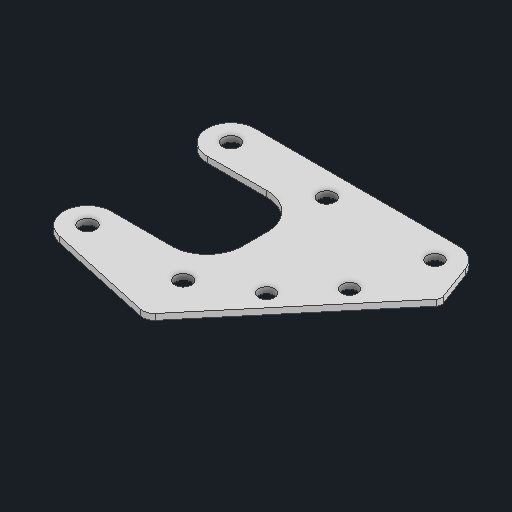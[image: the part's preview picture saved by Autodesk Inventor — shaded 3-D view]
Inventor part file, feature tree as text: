
AUTODESK INVENTOR PART (.ipt)
format: ipt  version: 2025 (Build 290162000, 162)  size: 137,728 bytes
history: native  units: in
note: dims shown in document units (in); Inventor stores cm internally (conversion verified against a paired STEP export)
features: other x3, extrude x1, sketch x1
ambient origin geometry x8: Origin, YZ Plane, XZ Plane, XY Plane, X Axis, Y Axis, Z Axis, Center Point
bodies: Solid1 (feature_tree)
feature tree (5):
  other  "Blocks"
  extrude  "Extrusion1"  Depth=0.125in
  sketch  "Sketch1"  dims[d0=0.164in d1=0.5in d6=0.375in d8=0.164in d9=0.0625in d10=0.0625in d11=0.0in d14=0.164in d15=0.615in d17=0.125in]
  other  "main"
  other  "main:1"
